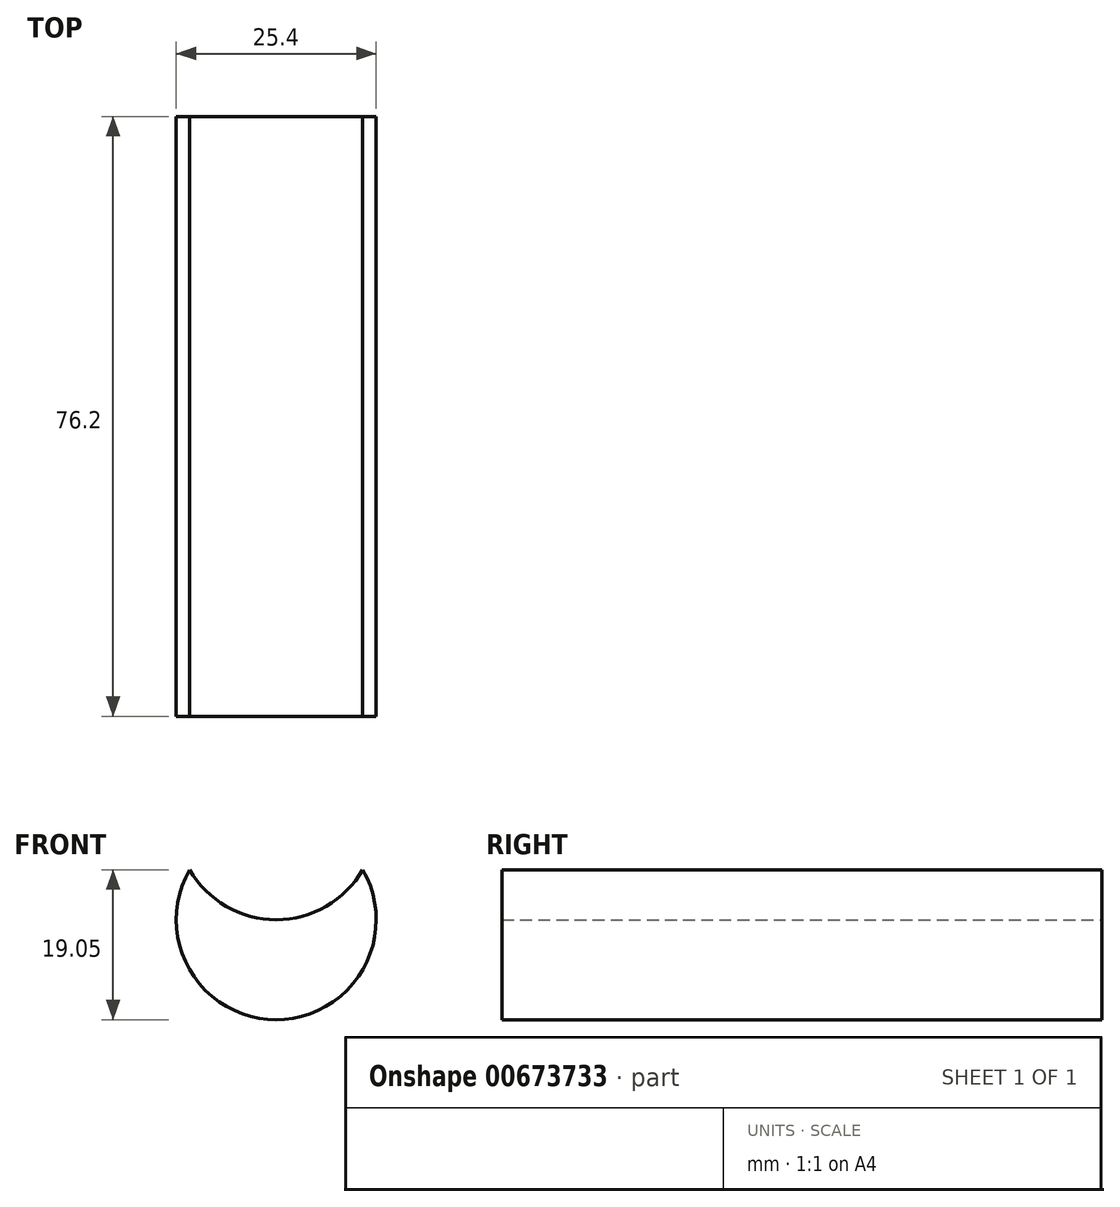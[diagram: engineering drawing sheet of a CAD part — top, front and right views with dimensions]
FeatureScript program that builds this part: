
annotation { "Feature Type Name" : "Feature", "Feature Type Description" : "" }
export const myFeature = defineFeature(function(context is Context, id is Id, definition is map)
    precondition{}
    {
        {
            var Q0;
            Q0=qCreatedBy(makeId("Front.planeOp"),FACE);
            var sketch = newSketch(context, id + "F0", { "sketchPlane" : qUnion([Q0])});
            skArc(sketch, "E0", {"start": v(-11, 6.35) * mm, "mid": v(0, -12.7) * mm, "end": v(11, 6.35) * mm});
            skArc(sketch, "E1", {"start": v(-11, 6.35) * mm, "mid": v(0, 0) * mm, "end": v(11, 6.35) * mm});
            skSolve(sketch);
        }
        {
            var Q0;
            Q0=makeQuery(id+"F0.imprint","IMPRINT",FACE,{"disambiguationData":[TD([[makeQuery(id+"F0.imprint","IMPRINT",EDGE,{"derivedFrom":sQuery(id+"F0.wireOp",EDGE,"E0")}),1.0]])]});
            extrude(context, id + "F1", {"entities" : qUnion([Q0]), "depth" : 76.2 * mm, "offsetDistance" : 25.4 * mm});
        }
    });
